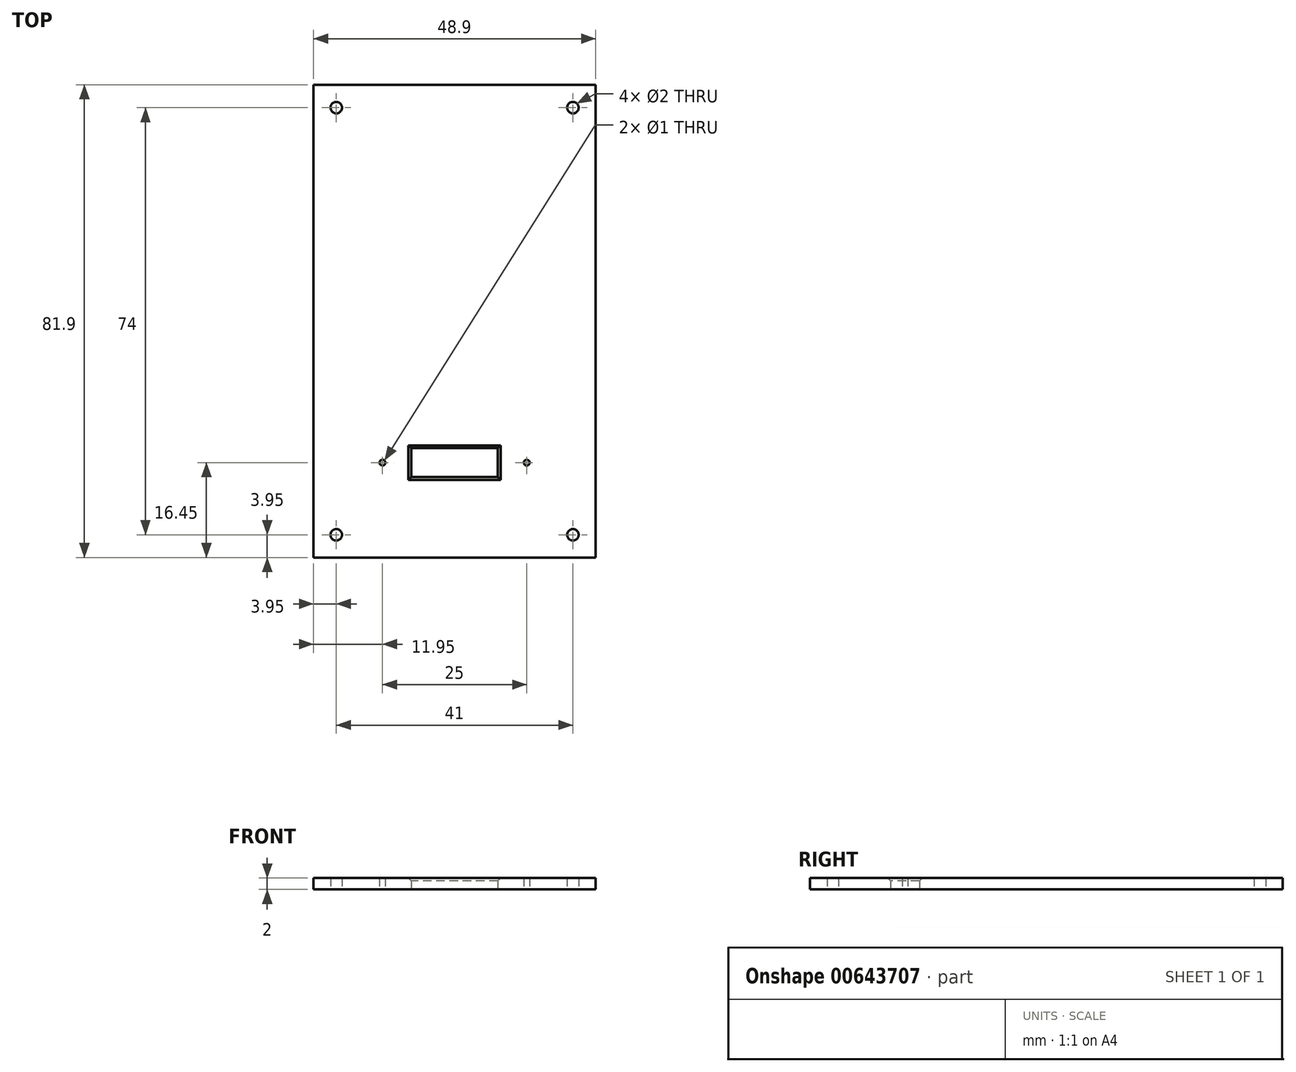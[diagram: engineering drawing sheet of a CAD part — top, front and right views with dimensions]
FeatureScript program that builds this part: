
annotation { "Feature Type Name" : "Feature", "Feature Type Description" : "" }
export const myFeature = defineFeature(function(context is Context, id is Id, definition is map)
    precondition{}
    {
        {
            var Q0;
            Q0=qCreatedBy(makeId("Top.planeOp"),FACE);
            var sketch = newSketch(context, id + "F0", { "sketchPlane" : qUnion([Q0])});
            skLineSegment(sketch, "E0.bottom", {"start": v(-24.45, 40.95) * mm, "end": v(24.45, 40.95) * mm});
            skLineSegment(sketch, "E0.top", {"start": v(-24.45, -40.95) * mm, "end": v(24.45, -40.95) * mm});
            skLineSegment(sketch, "E0.left", {"start": v(-24.45, 40.95) * mm, "end": v(-24.45, -40.95) * mm});
            skLineSegment(sketch, "E0.right", {"start": v(24.45, 40.95) * mm, "end": v(24.45, -40.95) * mm});
            skLineSegment(sketch, "E1.bottom", {"start": v(-20.5, 37) * mm, "end": v(20.5, 37) * mm, "construction": true});
            skLineSegment(sketch, "E1.top", {"start": v(-20.5, -37) * mm, "end": v(20.5, -37) * mm, "construction": true});
            skLineSegment(sketch, "E1.left", {"start": v(-20.5, 37) * mm, "end": v(-20.5, -37) * mm, "construction": true});
            skLineSegment(sketch, "E1.right", {"start": v(20.5, 37) * mm, "end": v(20.5, -37) * mm, "construction": true});
            skPoint(sketch, "E2", {"position": v(-20.5, 37) * mm});
            skPoint(sketch, "E3", {"position": v(20.5, 37) * mm});
            skPoint(sketch, "E4", {"position": v(-20.5, -37) * mm});
            skPoint(sketch, "E5", {"position": v(20.5, -37) * mm});
            skLineSegment(sketch, "E6.bottom", {"start": v(-7.5, -22) * mm, "end": v(7.5, -22) * mm});
            skLineSegment(sketch, "E6.top", {"start": v(-7.5, -27) * mm, "end": v(7.5, -27) * mm});
            skLineSegment(sketch, "E6.left", {"start": v(-7.5, -22) * mm, "end": v(-7.5, -27) * mm});
            skLineSegment(sketch, "E6.right", {"start": v(7.5, -22) * mm, "end": v(7.5, -27) * mm});
            skPoint(sketch, "E7", {"position": v(-12.5, -24.5) * mm});
            skPoint(sketch, "E8", {"position": v(12.5, -24.5) * mm});
            skSolve(sketch);
        }
        {
            var Q0;
            Q0=makeQuery(id+"F0.imprint","IMPRINT",FACE,{"disambiguationData":[TD([[makeQuery(id+"F0.imprint","IMPRINT",EDGE,{"derivedFrom":sQuery(id+"F0.wireOp",EDGE,"E0.bottom")}),-1.0]])]});
            extrude(context, id + "F1", {"entities" : qUnion([Q0]), "depth" : 2 * mm, "offsetDistance" : 25 * mm});
        }
        {
            var Q0;
            Q0=sQuery(id+"F0.wireOp",VERTEX,"E2");
            var Q1;
            Q1=sQuery(id+"F0.wireOp",VERTEX,"E3");
            var Q2;
            Q2=sQuery(id+"F0.wireOp",VERTEX,"E4");
            var Q3;
            Q3=sQuery(id+"F0.wireOp",VERTEX,"E5");
            var Q4;
            Q4=makeQuery(id+"F1.opExtrude","SWEPT_BODY",BODY,{"disambiguationData":[OSD([sQuery(id+"F0.wireOp",EDGE,"E0.bottom"),sQuery(id+"F0.wireOp",EDGE,"E0.top"),sQuery(id+"F0.wireOp",EDGE,"E0.left"),sQuery(id+"F0.wireOp",EDGE,"E0.right"),sQuery(id+"F0.wireOp",EDGE,"E6.bottom"),sQuery(id+"F0.wireOp",EDGE,"E6.top"),sQuery(id+"F0.wireOp",EDGE,"E6.left"),sQuery(id+"F0.wireOp",EDGE,"E6.right")])]});
            hole(context, id + "F2", {"style" : HoleStyle.SIMPLE, "endStyle" : HoleEndStyle.BLIND, "oppositeDirection" : true, "holeDiameter" : 2 * mm, "majorDiameter" : 5 * mm, "holeDepth" : 15 * mm, "isTappedThrough" : true, "tappedDepth" : 12 * mm, "tapClearance" : 3, "startFromSketch" : true, "locations" : qUnion([Q0, Q1, Q2, Q3]), "scope" : qUnion([Q4])});
        }
        {
            var Q0;
            Q0=sQuery(id+"F0.wireOp",VERTEX,"E7");
            var Q1;
            Q1=sQuery(id+"F0.wireOp",VERTEX,"E8");
            var Q2;
            Q2=makeQuery(id+"F1.opExtrude","SWEPT_BODY",BODY,{"disambiguationData":[OSD([sQuery(id+"F0.wireOp",EDGE,"E0.bottom"),sQuery(id+"F0.wireOp",EDGE,"E0.top"),sQuery(id+"F0.wireOp",EDGE,"E0.left"),sQuery(id+"F0.wireOp",EDGE,"E0.right"),sQuery(id+"F0.wireOp",EDGE,"E6.bottom"),sQuery(id+"F0.wireOp",EDGE,"E6.top"),sQuery(id+"F0.wireOp",EDGE,"E6.left"),sQuery(id+"F0.wireOp",EDGE,"E6.right")])]});
            hole(context, id + "F3", {"style" : HoleStyle.SIMPLE, "endStyle" : HoleEndStyle.BLIND, "oppositeDirection" : true, "holeDiameter" : 1 * mm, "majorDiameter" : 5 * mm, "holeDepth" : 15 * mm, "isTappedThrough" : true, "tappedDepth" : 12 * mm, "tapClearance" : 3, "startFromSketch" : true, "locations" : qUnion([Q0, Q1]), "scope" : qUnion([Q2])});
        }
        {
            var Q0;
            Q0=makeQuery(id+"F1.opExtrude","CAP_EDGE",EDGE,{"disambiguationData":[OSD([sQuery(id+"F0.wireOp",EDGE,"E6.bottom")])],"isStart":false});
            var Q1;
            Q1=makeQuery(id+"F1.opExtrude","CAP_EDGE",EDGE,{"disambiguationData":[OSD([sQuery(id+"F0.wireOp",EDGE,"E6.left")])],"isStart":false});
            var Q2;
            Q2=makeQuery(id+"F1.opExtrude","CAP_EDGE",EDGE,{"disambiguationData":[OSD([sQuery(id+"F0.wireOp",EDGE,"E6.top")])],"isStart":false});
            var Q3;
            Q3=makeQuery(id+"F1.opExtrude","CAP_EDGE",EDGE,{"disambiguationData":[OSD([sQuery(id+"F0.wireOp",EDGE,"E6.right")])],"isStart":false});
            chamfer(context, id + "F4", {"entities" : qUnion([Q0, Q1, Q2, Q3]), "width" : 0.5 * mm, "tangentPropagation" : true});
        }
    });
